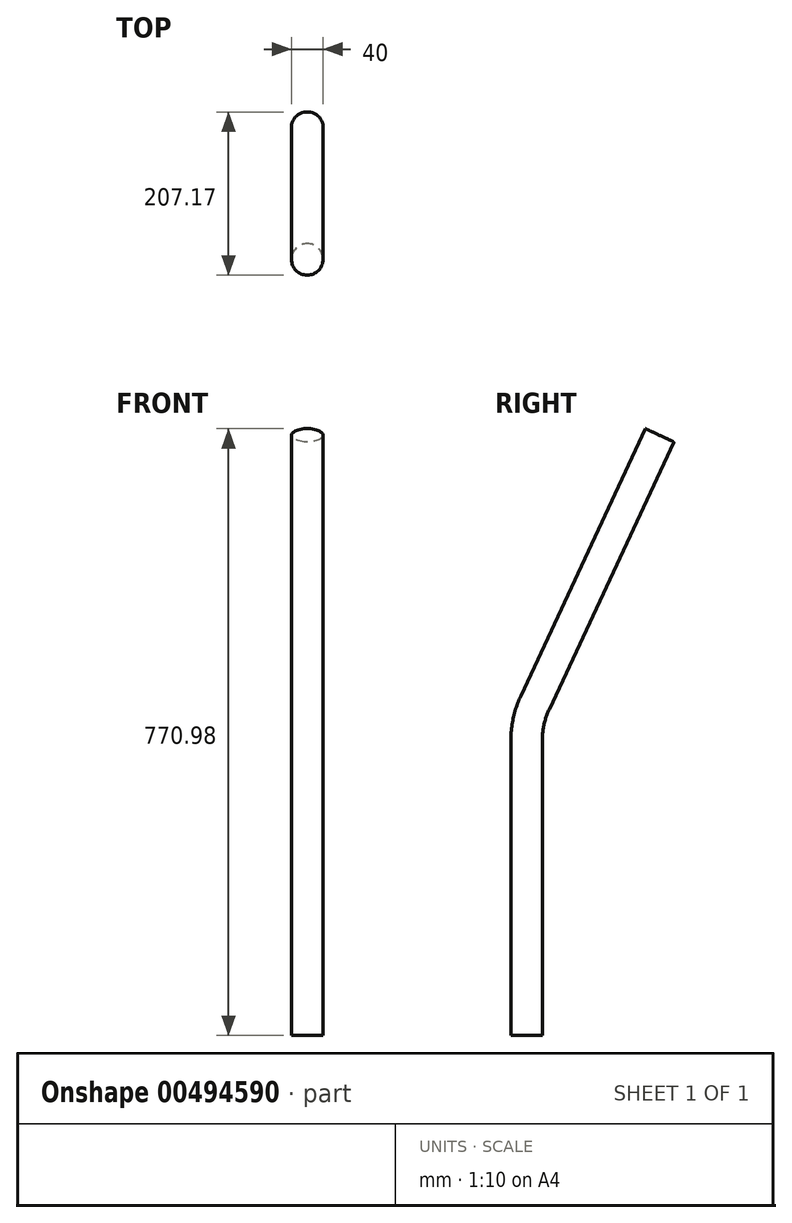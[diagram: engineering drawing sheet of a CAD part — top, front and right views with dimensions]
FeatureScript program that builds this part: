
annotation { "Feature Type Name" : "Feature", "Feature Type Description" : "" }
export const myFeature = defineFeature(function(context is Context, id is Id, definition is map)
    precondition{}
    {
        {
            var Q0;
            Q0=qCreatedBy(makeId("Right.planeOp"),FACE);
            var sketch = newSketch(context, id + "F0", { "sketchPlane" : qUnion([Q0])});
            skLineSegment(sketch, "E0", {"start": v(0, 0) * mm, "end": v(0, 374.73) * mm});
            skLineSegment(sketch, "E1", {"start": v(10.68, 422.9) * mm, "end": v(169.05, 762.52) * mm});
            skPoint(sketch, "E2.visualSharp", {"position": v(0, 400) * mm});
            skArc(sketch, "E2.filletArc", {"start": v(10.68, 422.9) * mm, "mid": v(2.7, 399.4) * mm, "end": v(0, 374.73) * mm});
            skSolve(sketch);
        }
        {
            var Q0;
            Q0=qCreatedBy(makeId("Top.planeOp"),FACE);
            var sketch = newSketch(context, id + "F1", { "sketchPlane" : qUnion([Q0])});
            skPoint(sketch, "E3.0", {"position": v(0, 0) * mm});
            skCircle(sketch, "E4", {"center": v(0, 0) * mm, "radius": 20 * mm});
            skSolve(sketch);
        }
        {
            var Q0;
            Q0=makeQuery(id+"F1.imprint","IMPRINT",FACE,{"disambiguationData":[TD([[makeQuery(id+"F1.imprint","IMPRINT",EDGE,{"derivedFrom":sQuery(id+"F1.wireOp",EDGE,"E4")}),1.0]])]});
            var Q1;
            Q1=sQuery(id+"F0.wireOp",EDGE,"E0");
            var Q2;
            Q2=sQuery(id+"F0.wireOp",EDGE,"E2.filletArc");
            var Q3;
            Q3=sQuery(id+"F0.wireOp",EDGE,"E1");
            sweep(context, id + "F2", {"profiles" : qUnion([Q0]), "path" : qUnion([Q1, Q2, Q3])});
        }
    });
